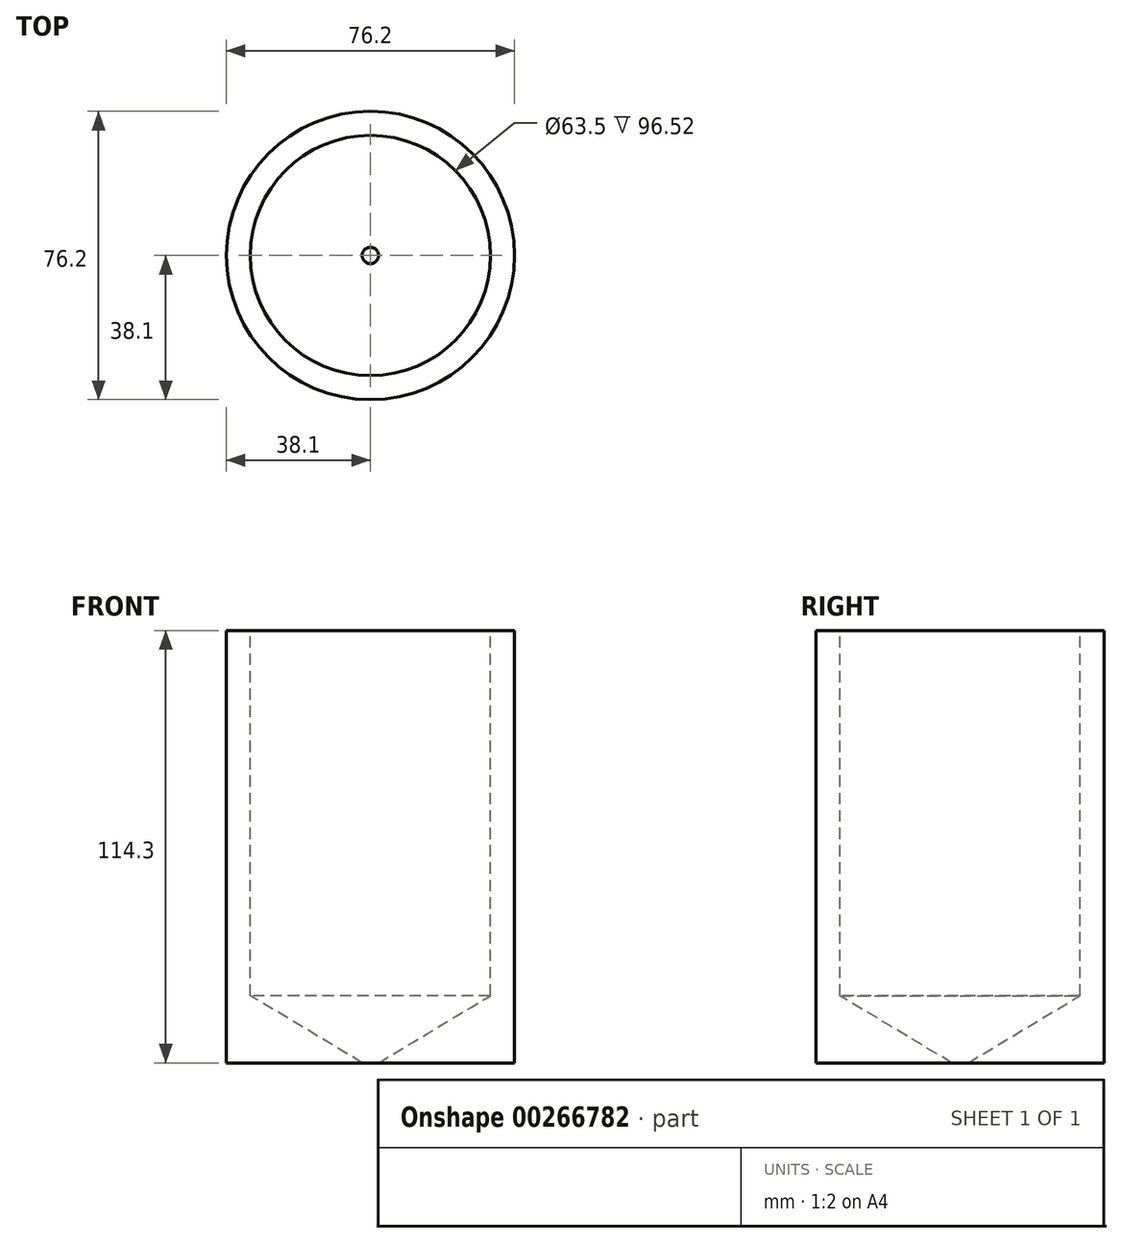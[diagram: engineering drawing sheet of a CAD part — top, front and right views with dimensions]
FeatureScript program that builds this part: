
annotation { "Feature Type Name" : "Feature", "Feature Type Description" : "" }
export const myFeature = defineFeature(function(context is Context, id is Id, definition is map)
    precondition{}
    {
        {
            var Q0;
            Q0=qCreatedBy(makeId("Top.planeOp"),FACE);
            var sketch = newSketch(context, id + "F0", { "sketchPlane" : qUnion([Q0])});
            skCircle(sketch, "E0", {"center": v(0, 0) * mm, "radius": 38.1 * mm});
            skSolve(sketch);
        }
        {
            var Q0;
            Q0=makeQuery(id+"F0.imprint","IMPRINT",FACE,{"disambiguationData":[TD([[makeQuery(id+"F0.imprint","IMPRINT",EDGE,{"derivedFrom":sQuery(id+"F0.wireOp",EDGE,"E0")}),1.0]])]});
            extrude(context, id + "F1", {"entities" : qUnion([Q0]), "depth" : 114.3 * mm});
        }
        {
            var Q0;
            Q0=makeQuery(id+"F1.opExtrude","CAP_FACE",FACE,{"disambiguationData":[OSD([sQuery(id+"F0.wireOp",EDGE,"E0")])],"isStart":false});
            var sketch = newSketch(context, id + "F2", { "sketchPlane" : qUnion([Q0])});
            skPoint(sketch, "E1", {"position": v(0, 0) * mm});
            skSolve(sketch);
        }
        {
            var Q0;
            Q0=sQuery(id+"F2.wireOp",VERTEX,"E1");
            var Q1;
            Q1=makeQuery(id+"F1.opExtrude","SWEPT_BODY",BODY,{"disambiguationData":[OSD([sQuery(id+"F0.wireOp",EDGE,"E0")])]});
            hole(context, id + "F3", {"style" : HoleStyle.SIMPLE, "endStyle" : HoleEndStyle.BLIND, "holeDiameter" : 63.5 * mm, "holeDepth" : 96.52 * mm, "tappedDepth" : 12.7 * mm, "tapClearance" : 3, "locations" : qUnion([Q0]), "scope" : qUnion([Q1])});
        }
    });
